# Revit family: DC_Holyoake_OutsideLouver_OHL-F-124_supply_13
name_source: partatom
category: Air Terminals
revit_build: Autodesk Revit 2014 (Build: 20130308_1515(x64)
units: mm (PartAtom-declared; Revit-internal decimal feet)

## types (1)
- OHL-F-124
    Accessories = Aluminium Bird mesh or insect mesh (fibreglass)
    Blade Array Count = 9.619423
    Blade Count = 9
    Blade Cut Setout = 685.8 mm
    Blade Height = 89.8 mm
    Blade Length = 653 mm  [stored 2.14239 ft]
    Blade Offset = 4.63 mm
    Blade Pitch = 76.2 mm  [stored 0.25 ft]
    Blade Width = 97.1 mm  [stored 0.31857 ft]
    Connector Height = 709 mm
    Connector Width = 629 mm
    Description = Weather Louvres shall be Holyoake Model OHL-F-124 straight profile 76mm louvred blades set at 76mm centres and constructed in a 45mm flanged (F) frame to suit the installation profile.  Weather Louvres shall be of extruded aluminium construction and finished in natural anodised or powdercoat and fitted with accessories and dampers where indicated as manufactured by Holyoake.
    Exact Neck Height = 780 mm  [stored 2.55906 ft]
    Exact Neck Width = 700 mm  [stored 2.29659 ft]
    Exact Overall Flange Height = 830.8 mm  [stored 2.72572 ft]
    Exact Overall Flange Width = 750.8 mm  [stored 2.46325 ft]
    Flange Width = 25.4 mm  [stored 0.0833333 ft]
    Holyoake Product Range = Outside Louvres
    Louver Depth = 106.35 mm  [stored 0.348917 ft]
    Manufacturer = Holyoake
    Material - Body = Holyoake Aluminium
    Material - Face = Holyoake Aluminium
    Max Flow = 2000.0 L/s
    Min Flow = 100.0 L/s
    Model = OHL-F-124
    Noise Level NC Max = 0.00 NC
    Noise Level NC Min = 0.00 NC
    Nominal Height = 786 mm  [stored 2.57874 ft]
    Nominal Width = 706 mm
    Overall Depth = 38.3 mm
    Overall Opening = 733 mm  [stored 2.40486 ft]
    Static Pressure Max = 0.0 Pa
    Static Pressure Min = 0.0 Pa
    Top Blade Height = 47.2 mm
    Type Comments = 76mm Horizontal Straight Profile Louvers in Flanged Surround
    URL = http://www.holyoake.com

note: [stored X ft] marks values corroborated as IEEE doubles in the binary element streams (Revit-internal decimal feet)

## geometry (parser evidence)
native form markers: Blend x6, Sweep x8
no freeform markers — native parametric forms only
